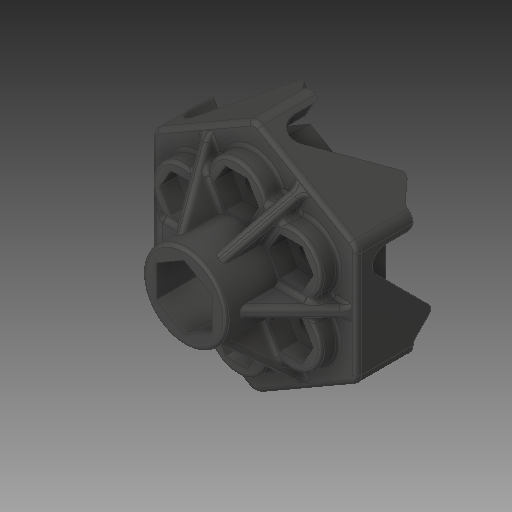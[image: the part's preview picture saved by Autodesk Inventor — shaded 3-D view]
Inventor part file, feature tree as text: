
AUTODESK INVENTOR PART (.ipt)
format: ipt  version: 2018 (Build 220112000, 112)  size: 1,369,600 bytes
history: native  units: in
note: dims shown in document units (in); Inventor stores cm internally (conversion verified against a paired STEP export)
features: fillet x1
ambient origin geometry x8: Origin, YZ Plane, XZ Plane, XY Plane, X Axis, Y Axis, Z Axis, Center Point
bodies: Solid1 (feature_tree)
feature tree (1):
  fillet  "Fillet21"  [1 undecoded]
note: 1 required parameter value undecoded (feature->parameter linkage not recoverable at this tier; creation-order binding heuristic only, values carry confidence <= 0.55)
